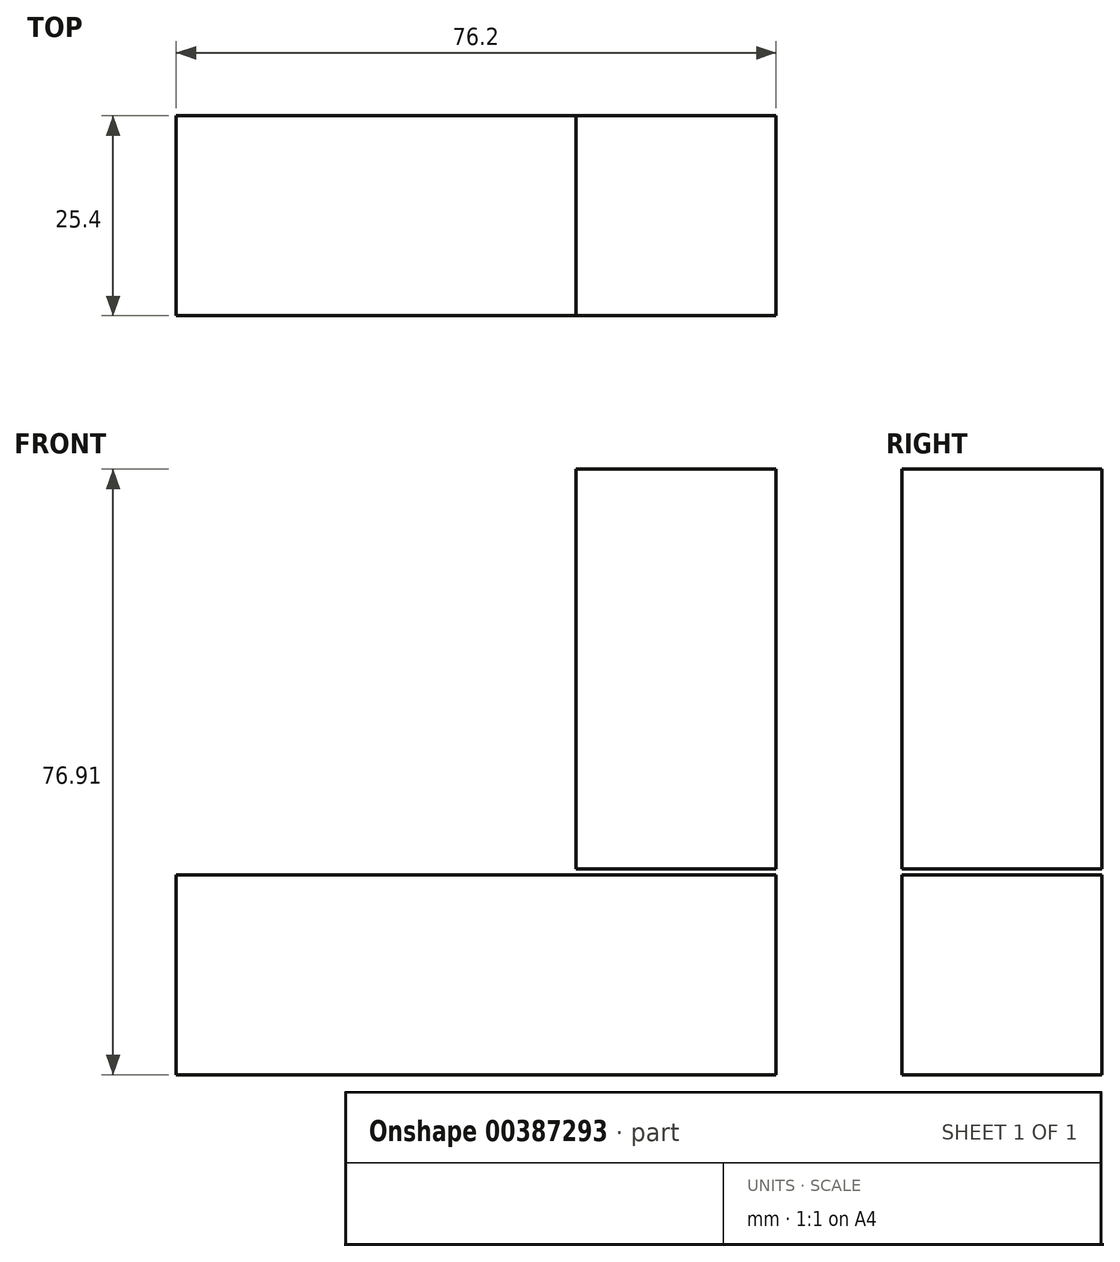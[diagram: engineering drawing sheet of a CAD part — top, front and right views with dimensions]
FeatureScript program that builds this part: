
annotation { "Feature Type Name" : "Feature", "Feature Type Description" : "" }
export const myFeature = defineFeature(function(context is Context, id is Id, definition is map)
    precondition{}
    {
        {
            var Q0;
            Q0=qCreatedBy(makeId("Front.planeOp"),FACE);
            var sketch = newSketch(context, id + "F0", { "sketchPlane" : qUnion([Q0])});
            skLineSegment(sketch, "E0.bottom", {"start": v(0, 0) * mm, "end": v(25.4, 0) * mm});
            skLineSegment(sketch, "E0.top", {"start": v(0, 25.4) * mm, "end": v(25.4, 25.4) * mm});
            skLineSegment(sketch, "E0.left", {"start": v(0, 0) * mm, "end": v(0, 25.4) * mm});
            skLineSegment(sketch, "E0.right", {"start": v(25.4, 0) * mm, "end": v(25.4, 25.4) * mm});
            skLineSegment(sketch, "E1.bottom", {"start": v(0, 0) * mm, "end": v(-25.4, 0) * mm});
            skLineSegment(sketch, "E1.top", {"start": v(0, 25.4) * mm, "end": v(-25.4, 25.4) * mm});
            skLineSegment(sketch, "E1.right", {"start": v(-25.4, 0) * mm, "end": v(-25.4, 25.4) * mm});
            skLineSegment(sketch, "E2.bottom", {"start": v(-25.4, 0) * mm, "end": v(-50.8, 0) * mm});
            skLineSegment(sketch, "E2.top", {"start": v(-25.4, 25.4) * mm, "end": v(-50.8, 25.4) * mm});
            skLineSegment(sketch, "E2.right", {"start": v(-50.8, 0) * mm, "end": v(-50.8, 25.4) * mm});
            skSolve(sketch);
        }
        {
            var Q0;
            Q0=qCreatedBy(makeId("Front.planeOp"),FACE);
            var sketch = newSketch(context, id + "F1", { "sketchPlane" : qUnion([Q0])});
            skLineSegment(sketch, "E3.bottom", {"start": v(0, 26.1) * mm, "end": v(25.4, 26.1) * mm});
            skLineSegment(sketch, "E3.top", {"start": v(0, 51.5) * mm, "end": v(25.4, 51.5) * mm});
            skLineSegment(sketch, "E3.left", {"start": v(0, 26.1) * mm, "end": v(0, 51.5) * mm});
            skLineSegment(sketch, "E3.right", {"start": v(25.4, 26.1) * mm, "end": v(25.4, 51.5) * mm});
            skLineSegment(sketch, "E4.top", {"start": v(0, 76.9) * mm, "end": v(25.4, 76.9) * mm});
            skLineSegment(sketch, "E4.left", {"start": v(0, 51.5) * mm, "end": v(0, 76.9) * mm});
            skLineSegment(sketch, "E4.right", {"start": v(25.4, 51.5) * mm, "end": v(25.4, 76.9) * mm});
            skSolve(sketch);
        }
        {
            var Q0;
            Q0=makeQuery(id+"F1.imprint","IMPRINT",FACE,{"disambiguationData":[TD([[makeQuery(id+"F1.imprint","IMPRINT",EDGE,{"derivedFrom":sQuery(id+"F1.wireOp",EDGE,"E3.top")}),1.0]])]});
            var Q1;
            Q1=makeQuery(id+"F1.imprint","IMPRINT",FACE,{"disambiguationData":[TD([[makeQuery(id+"F1.imprint","IMPRINT",EDGE,{"derivedFrom":sQuery(id+"F1.wireOp",EDGE,"E3.bottom")}),1.0]])]});
            var Q2;
            Q2=makeQuery(id+"F0.imprint","IMPRINT",FACE,{"disambiguationData":[TD([[makeQuery(id+"F0.imprint","IMPRINT",EDGE,{"derivedFrom":sQuery(id+"F0.wireOp",EDGE,"E0.bottom")}),1.0]])]});
            var Q3;
            Q3=makeQuery(id+"F0.imprint","IMPRINT",FACE,{"disambiguationData":[TD([[makeQuery(id+"F0.imprint","IMPRINT",EDGE,{"derivedFrom":sQuery(id+"F0.wireOp",EDGE,"E1.bottom")}),-1.0]])]});
            var Q4;
            Q4=makeQuery(id+"F0.imprint","IMPRINT",FACE,{"disambiguationData":[TD([[makeQuery(id+"F0.imprint","IMPRINT",EDGE,{"derivedFrom":sQuery(id+"F0.wireOp",EDGE,"E2.bottom")}),-1.0]])]});
            extrude(context, id + "F2", {"entities" : qUnion([Q0, Q1, Q2, Q3, Q4]), "depth" : 25.4 * mm});
        }
    });
